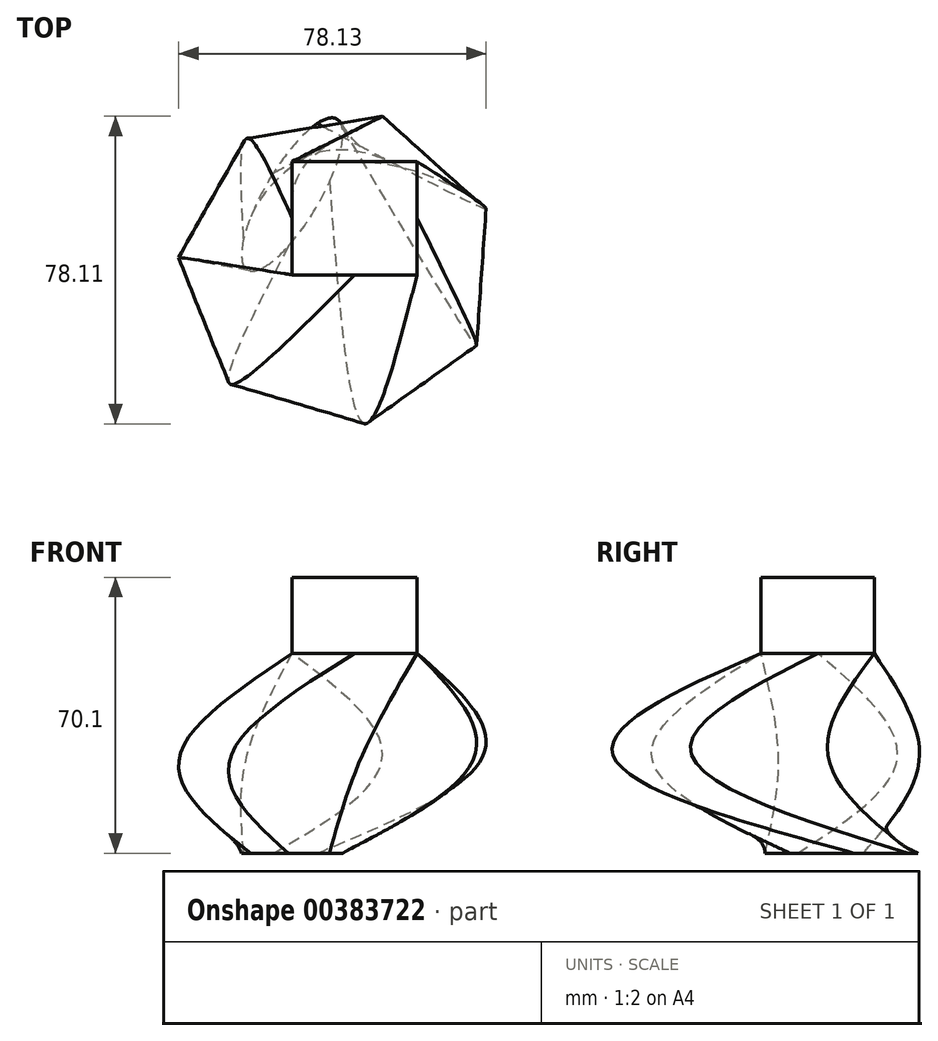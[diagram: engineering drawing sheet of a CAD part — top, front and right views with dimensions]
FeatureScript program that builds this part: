
annotation { "Feature Type Name" : "Feature", "Feature Type Description" : "" }
export const myFeature = defineFeature(function(context is Context, id is Id, definition is map)
    precondition{}
    {
        {
            var Q0;
            Q0=qCreatedBy(makeId("Top.planeOp"),FACE);
            var sketch = newSketch(context, id + "F0", { "sketchPlane" : qUnion([Q0])});
            skEllipse(sketch, "E0", {"center": v(0, 0) * mm, "majorRadius": 22.28 * mm, "minorRadius": 6.92 * mm, "majorAxis": v(-0.51, -0.86)});
            skSolve(sketch);
        }
        {
            var Q0;
            Q0=qCreatedBy(makeId("Top.planeOp"),FACE);
            cPlane(context, id + "F1", {"entities" : qUnion([Q0]), "cplaneType" : CPlaneType.OFFSET, "offset" : 25.4 * mm, "width" : 152.4 * mm, "height" : 152.4 * mm});
        }
        {
            var Q0;
            Q0=qCreatedBy(id+"F1.planeOp",FACE);
            var sketch = newSketch(context, id + "F2", { "sketchPlane" : qUnion([Q0])});
            skCircle(sketch, "E1.cCircle", {"center": v(11.63, -18.59) * mm, "radius": 36.11 * mm, "construction": true});
            skLineSegment(sketch, "E1.0", {"start": v(-15.3, -48.28) * mm, "end": v(-28.37, -16.05) * mm});
            skLineSegment(sketch, "E1.1", {"start": v(-28.37, -16.05) * mm, "end": v(-11.32, 14.27) * mm});
            skLineSegment(sketch, "E1.2", {"start": v(-11.32, 14.27) * mm, "end": v(23, 19.84) * mm});
            skLineSegment(sketch, "E1.3", {"start": v(23, 19.84) * mm, "end": v(48.77, -3.52) * mm});
            skLineSegment(sketch, "E1.4", {"start": v(48.77, -3.52) * mm, "end": v(46.57, -38.23) * mm});
            skLineSegment(sketch, "E1.5", {"start": v(46.57, -38.23) * mm, "end": v(18.05, -58.15) * mm});
            skLineSegment(sketch, "E1.6", {"start": v(18.05, -58.15) * mm, "end": v(-15.3, -48.28) * mm});
            skPoint(sketch, "E1.0.midPoint", {"position": v(-21.83, -32.16) * mm});
            skSolve(sketch);
        }
        {
            var Q0;
            Q0=qCreatedBy(id+"F1.planeOp",FACE);
            cPlane(context, id + "F3", {"entities" : qUnion([Q0]), "cplaneType" : CPlaneType.OFFSET, "offset" : 25.4 * mm, "width" : 152.4 * mm, "height" : 152.4 * mm});
        }
        {
            var Q0;
            Q0=qCreatedBy(id+"F3.planeOp",FACE);
            var sketch = newSketch(context, id + "F4", { "sketchPlane" : qUnion([Q0])});
            skLineSegment(sketch, "E2.bottom", {"start": v(0, 8.36) * mm, "end": v(31.73, 8.36) * mm});
            skLineSegment(sketch, "E2.top", {"start": v(0, -20.43) * mm, "end": v(31.73, -20.43) * mm});
            skLineSegment(sketch, "E2.left", {"start": v(0, 8.36) * mm, "end": v(0, -20.43) * mm});
            skLineSegment(sketch, "E2.right", {"start": v(31.73, 8.36) * mm, "end": v(31.73, -20.43) * mm});
            skSolve(sketch);
        }
        {
            var Q0;
            Q0=makeQuery(id+"F0.imprint","IMPRINT",FACE,{"disambiguationData":[TD([[makeQuery(id+"F0.imprint","IMPRINT",EDGE,{"derivedFrom":sQuery(id+"F0.wireOp",EDGE,"E0")}),1.0]])]});
            var Q1;
            Q1=makeQuery(id+"F2.imprint","IMPRINT",FACE,{"disambiguationData":[TD([[makeQuery(id+"F2.imprint","IMPRINT",EDGE,{"derivedFrom":sQuery(id+"F2.wireOp",EDGE,"E1.0")}),-1.0]])]});
            var Q2;
            Q2=makeQuery(id+"F4.imprint","IMPRINT",FACE,{"disambiguationData":[TD([[makeQuery(id+"F4.imprint","IMPRINT",EDGE,{"derivedFrom":sQuery(id+"F4.wireOp",EDGE,"E2.bottom")}),-1.0]])]});
            loft(context, id + "F5", {"sheetProfilesArray" : [{ "sheetProfileEntities" : qUnion([Q0]) }, { "sheetProfileEntities" : qUnion([Q1]) }, { "sheetProfileEntities" : qUnion([Q2]) }]});
        }
        {
            var Q0;
            Q0=makeQuery(id+"F5.opLoft","CAP_FACE",FACE,{"disambiguationData":[OSD([makeQuery(id+"F4.imprint","IMPRINT",FACE,{"disambiguationData":[TD([[makeQuery(id+"F4.imprint","IMPRINT",EDGE,{"derivedFrom":sQuery(id+"F4.wireOp",EDGE,"E2.bottom")}),-1.0]])]})])],"isStart":true});
            extrude(context, id + "F6", {"entities" : qUnion([Q0]), "operationType" : NewBodyOperationType.ADD, "depth" : 19.3 * mm});
        }
    });
